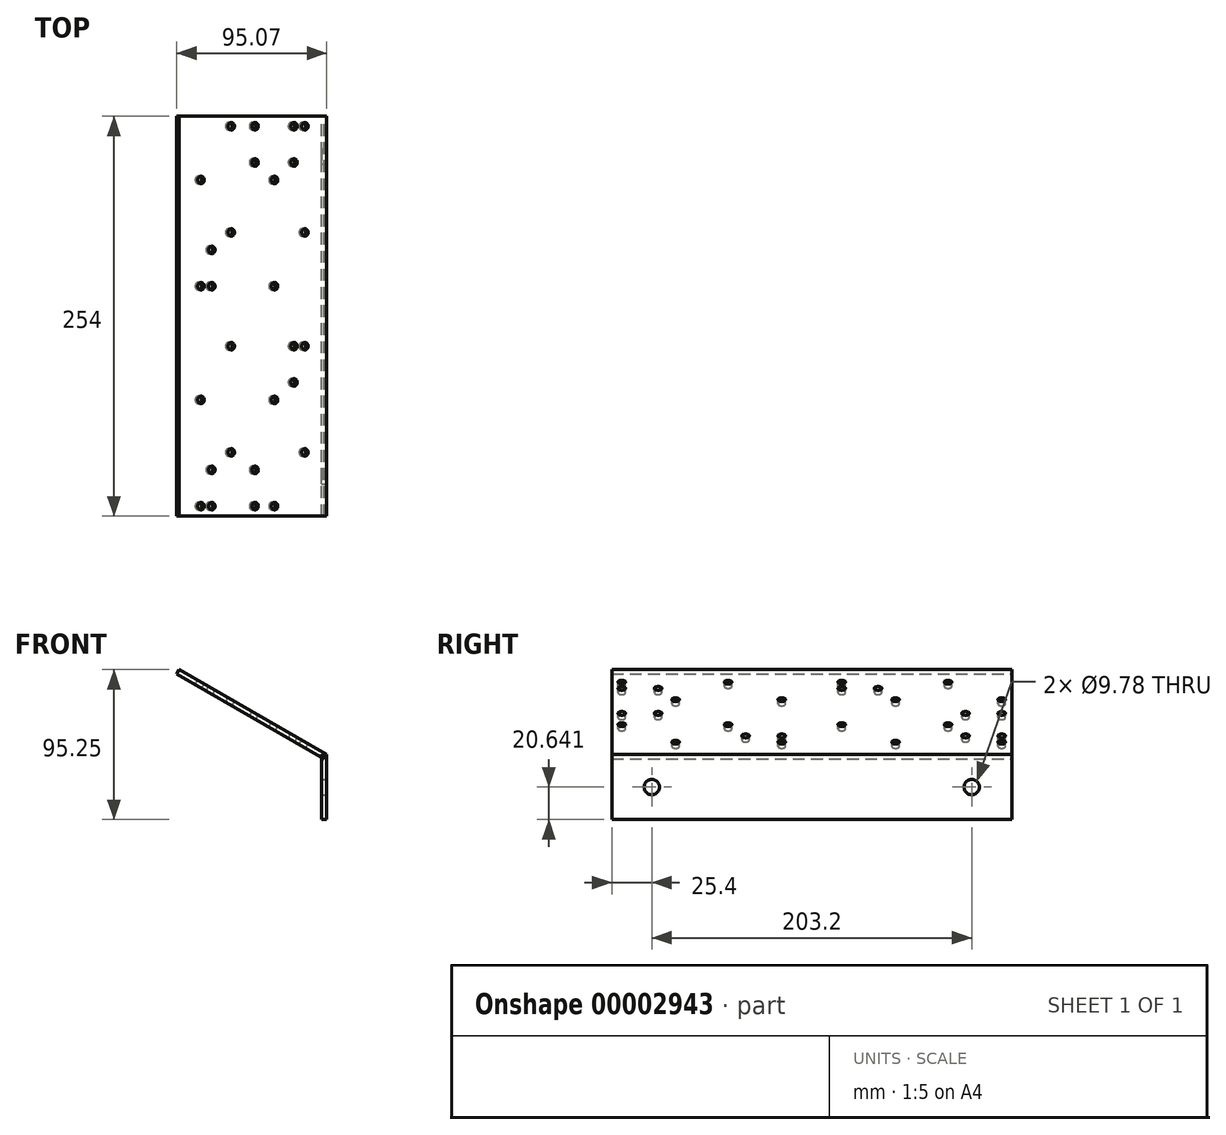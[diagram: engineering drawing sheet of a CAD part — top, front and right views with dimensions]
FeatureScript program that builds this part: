
annotation { "Feature Type Name" : "Feature", "Feature Type Description" : "" }
export const myFeature = defineFeature(function(context is Context, id is Id, definition is map)
    precondition{}
    {
        {
            var Q0;
            Q0=qCreatedBy(makeId("Right.planeOp"),FACE);
            var sketch = newSketch(context, id + "F0", { "sketchPlane" : qUnion([Q0])});
            skLineSegment(sketch, "E0.rect.bottom", {"start": v(-127, 52.45) * mm, "end": v(127, 52.45) * mm});
            skLineSegment(sketch, "E0.rect.top", {"start": v(-127, -55.5) * mm, "end": v(127, -55.5) * mm});
            skLineSegment(sketch, "E0.rect.left", {"start": v(-127, 52.45) * mm, "end": v(-127, -55.5) * mm});
            skLineSegment(sketch, "E0.rect.right", {"start": v(127, 52.45) * mm, "end": v(127, -55.5) * mm});
            skPoint(sketch, "E0.rect.middle", {"position": v(0, 0) * mm});
            skLineSegment(sketch, "E1.rect.top", {"start": v(-127, -96.78) * mm, "end": v(127, -96.78) * mm});
            skLineSegment(sketch, "E1.rect.left", {"start": v(-127, -55.5) * mm, "end": v(-127, -96.78) * mm});
            skLineSegment(sketch, "E1.rect.right", {"start": v(127, -55.5) * mm, "end": v(127, -96.78) * mm});
            skPoint(sketch, "E1.rect.middle", {"position": v(0, -76.14) * mm});
            skCircle(sketch, "E2", {"center": v(-101.6, -76.14) * mm, "radius": 4.89 * mm});
            skCircle(sketch, "E3", {"center": v(101.6, -76.14) * mm, "radius": 4.89 * mm});
            skCircle(sketch, "E4", {"center": v(86.52, 36.57) * mm, "radius": 2.38 * mm});
            skLineSegment(sketch, "E5", {"start": v(-127, 36.57) * mm, "end": v(127, 36.57) * mm, "construction": true});
            skLineSegment(sketch, "E6", {"start": v(-127, 28.64) * mm, "end": v(127, 28.64) * mm, "construction": true});
            skLineSegment(sketch, "E7", {"start": v(-127, 14.35) * mm, "end": v(127, 14.35) * mm, "construction": true});
            skLineSegment(sketch, "E8", {"start": v(-127, -3.11) * mm, "end": v(127, -3.11) * mm, "construction": true});
            skLineSegment(sketch, "E9", {"start": v(-127, -17.4) * mm, "end": v(127, -17.4) * mm, "construction": true});
            skLineSegment(sketch, "E10", {"start": v(-127, -39.63) * mm, "end": v(127, -39.63) * mm, "construction": true});
            skLineSegment(sketch, "E11", {"start": v(-127, -31.69) * mm, "end": v(127, -31.69) * mm, "construction": true});
            skCircle(sketch, "E12", {"center": v(19.05, 36.57) * mm, "radius": 2.38 * mm});
            skCircle(sketch, "E13", {"center": v(19.05, 28.64) * mm, "radius": 2.38 * mm});
            skCircle(sketch, "E14", {"center": v(42.07, 28.64) * mm, "radius": 2.38 * mm});
            skCircle(sketch, "E15", {"center": v(53.18, 14.35) * mm, "radius": 2.38 * mm});
            skCircle(sketch, "E16", {"center": v(120.65, 14.35) * mm, "radius": 2.38 * mm});
            skCircle(sketch, "E17", {"center": v(97.63, -3.11) * mm, "radius": 2.38 * mm});
            skCircle(sketch, "E18", {"center": v(120.65, -3.11) * mm, "radius": 2.38 * mm});
            skCircle(sketch, "E19", {"center": v(19.05, -17.4) * mm, "radius": 2.38 * mm});
            skCircle(sketch, "E20", {"center": v(86.52, -17.4) * mm, "radius": 2.38 * mm});
            skCircle(sketch, "E21", {"center": v(97.63, -31.69) * mm, "radius": 2.38 * mm});
            skCircle(sketch, "E22", {"center": v(120.65, -31.69) * mm, "radius": 2.38 * mm});
            skCircle(sketch, "E23", {"center": v(120.65, -39.63) * mm, "radius": 2.38 * mm});
            skCircle(sketch, "E24", {"center": v(53.18, -39.63) * mm, "radius": 2.38 * mm});
            skCircle(sketch, "E25", {"center": v(-120.65, 36.57) * mm, "radius": 2.38 * mm});
            skCircle(sketch, "E26", {"center": v(-53.18, 36.57) * mm, "radius": 2.38 * mm});
            skCircle(sketch, "E27", {"center": v(-120.65, 28.64) * mm, "radius": 2.38 * mm});
            skCircle(sketch, "E28", {"center": v(-97.63, 28.64) * mm, "radius": 2.38 * mm});
            skCircle(sketch, "E29", {"center": v(-86.52, 14.35) * mm, "radius": 2.38 * mm});
            skCircle(sketch, "E30", {"center": v(-19.05, 14.35) * mm, "radius": 2.38 * mm});
            skCircle(sketch, "E31", {"center": v(-120.65, -3.11) * mm, "radius": 2.38 * mm});
            skCircle(sketch, "E32", {"center": v(-97.63, -3.11) * mm, "radius": 2.38 * mm});
            skCircle(sketch, "E33", {"center": v(-53.18, -17.4) * mm, "radius": 2.38 * mm});
            skCircle(sketch, "E34", {"center": v(-120.65, -17.4) * mm, "radius": 2.38 * mm});
            skCircle(sketch, "E35", {"center": v(-19.05, -31.69) * mm, "radius": 2.38 * mm});
            skCircle(sketch, "E36", {"center": v(-42.07, -31.69) * mm, "radius": 2.38 * mm});
            skCircle(sketch, "E37", {"center": v(-86.52, -39.63) * mm, "radius": 2.38 * mm});
            skCircle(sketch, "E38", {"center": v(-19.05, -39.63) * mm, "radius": 2.38 * mm});
            skLineSegment(sketch, "E39", {"start": v(-120.65, 52.45) * mm, "end": v(-120.65, -55.5) * mm, "construction": true});
            skLineSegment(sketch, "E40", {"start": v(-97.63, 52.45) * mm, "end": v(-97.63, -55.5) * mm, "construction": true});
            skLineSegment(sketch, "E41", {"start": v(-86.52, 52.45) * mm, "end": v(-86.52, -55.5) * mm, "construction": true});
            skLineSegment(sketch, "E42", {"start": v(-53.18, 52.45) * mm, "end": v(-53.18, -55.5) * mm, "construction": true});
            skLineSegment(sketch, "E43", {"start": v(-42.07, 52.45) * mm, "end": v(-42.07, -55.5) * mm, "construction": true});
            skLineSegment(sketch, "E44", {"start": v(-19.05, 52.45) * mm, "end": v(-19.05, -55.5) * mm, "construction": true});
            skLineSegment(sketch, "E45", {"start": v(19.05, 52.45) * mm, "end": v(19.05, -55.5) * mm, "construction": true});
            skLineSegment(sketch, "E46", {"start": v(42.07, 52.45) * mm, "end": v(42.07, -55.5) * mm, "construction": true});
            skLineSegment(sketch, "E47", {"start": v(53.18, 52.45) * mm, "end": v(53.18, -55.5) * mm, "construction": true});
            skLineSegment(sketch, "E48", {"start": v(86.52, 52.45) * mm, "end": v(86.52, -55.5) * mm, "construction": true});
            skLineSegment(sketch, "E49", {"start": v(97.63, -55.5) * mm, "end": v(97.63, 52.45) * mm, "construction": true});
            skLineSegment(sketch, "E50", {"start": v(120.65, -55.5) * mm, "end": v(120.65, 52.45) * mm, "construction": true});
            skSolve(sketch);
        }
        {
            var Q0;
            Q0=makeQuery(id+"F0.imprint","IMPRINT",FACE,{"disambiguationData":[TD([[makeQuery(id+"F0.imprint","IMPRINT",EDGE,{"derivedFrom":sQuery(id+"F0.wireOp",EDGE,"E0.rect.top")}),-1.0]])]});
            extrude(context, id + "F1", {"entities" : qUnion([Q0]), "oppositeDirection" : true, "depth" : 3.17 * mm});
        }
        {
            var Q0;
            Q0=makeQuery(id+"F0.imprint","IMPRINT",FACE,{"disambiguationData":[TD([[makeQuery(id+"F0.imprint","IMPRINT",EDGE,{"derivedFrom":sQuery(id+"F0.wireOp",EDGE,"E0.rect.bottom")}),-1.0]])]});
            extrude(context, id + "F2", {"entities" : qUnion([Q0]), "oppositeDirection" : true, "depth" : 3.17 * mm});
        }
        {
            var Q0;
            Q0=makeQuery(id+"F2.opExtrude","SWEPT_BODY",BODY,{"disambiguationData":[OSD([sQuery(id+"F0.wireOp",EDGE,"E0.rect.bottom"),sQuery(id+"F0.wireOp",EDGE,"E0.rect.left"),sQuery(id+"F0.wireOp",EDGE,"E0.rect.right"),sQuery(id+"F0.wireOp",EDGE,"E0.rect.top")])]});
            var Q1;
            Q1=makeQuery(id+"F1.opExtrude","CAP_EDGE",EDGE,{"disambiguationData":[OSD([sQuery(id+"F0.wireOp",EDGE,"E0.rect.top")])],"isStart":true});
            transform(context, id + "F3", {"entities" : qUnion([Q0]), "transformType" : TransformType.ROTATION, "transformAxis" : qUnion([Q1]), "angle" : 60 * degree, "oppositeDirection" : true, "makeCopy" : false});
        }
    });
